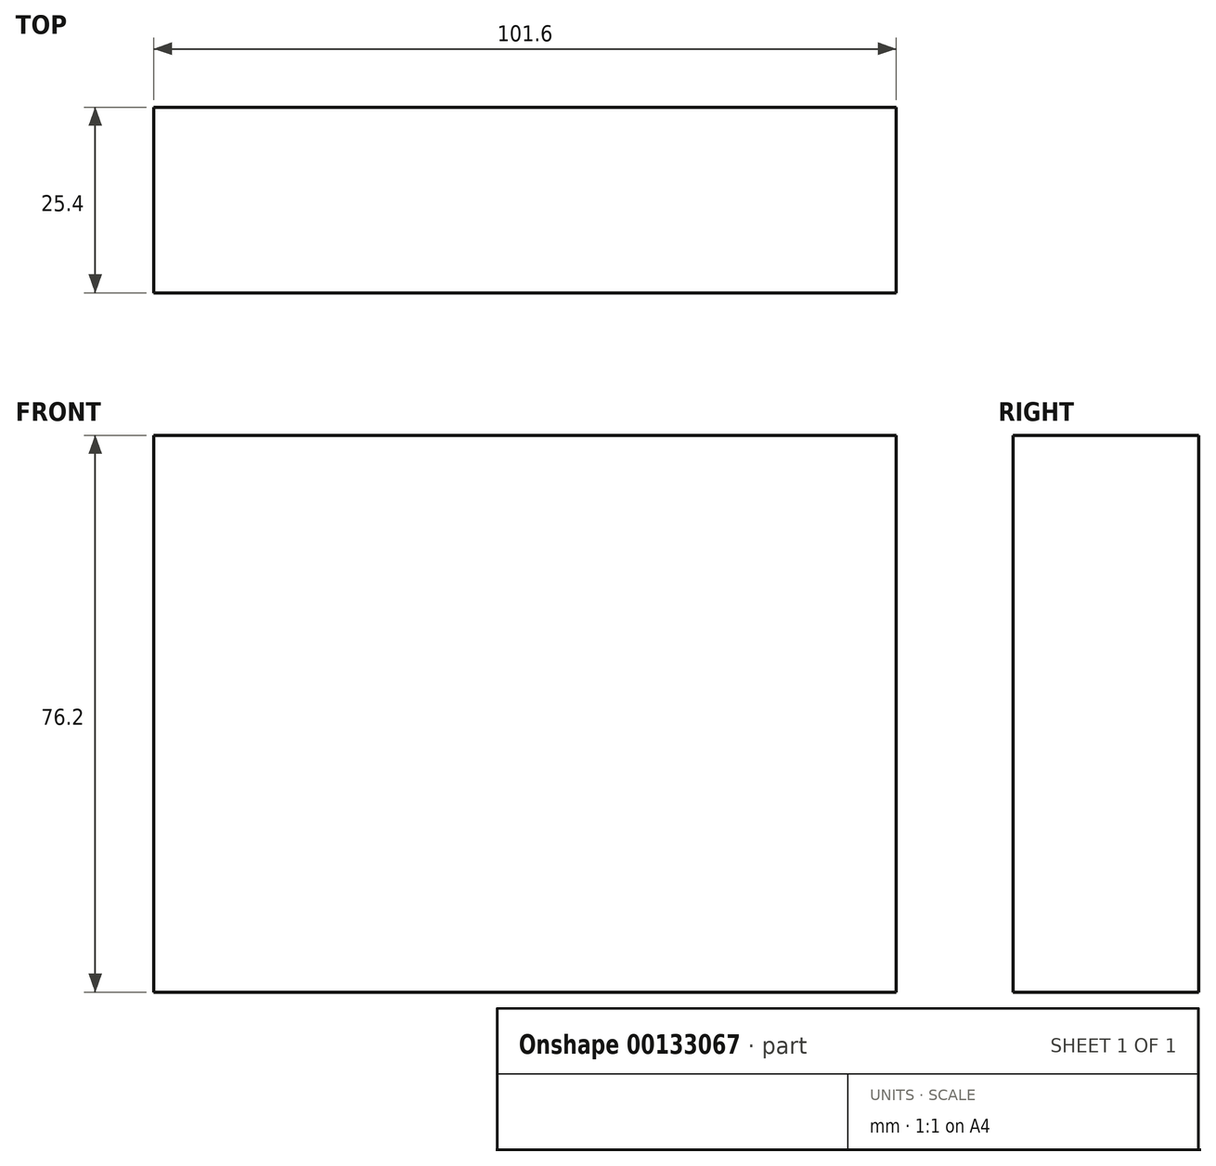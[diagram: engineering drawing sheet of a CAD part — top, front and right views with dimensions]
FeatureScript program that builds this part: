
annotation { "Feature Type Name" : "Feature", "Feature Type Description" : "" }
export const myFeature = defineFeature(function(context is Context, id is Id, definition is map)
    precondition{}
    {
        {
            var Q0;
            Q0=qCreatedBy(makeId("Front.planeOp"),FACE);
            var sketch = newSketch(context, id + "F0", { "sketchPlane" : qUnion([Q0])});
            skLineSegment(sketch, "E0.bottom", {"start": v(39.86, -22.03) * mm, "end": v(-61.74, -22.03) * mm});
            skLineSegment(sketch, "E0.top", {"start": v(39.86, 54.17) * mm, "end": v(-61.74, 54.17) * mm});
            skLineSegment(sketch, "E0.left", {"start": v(39.86, -22.03) * mm, "end": v(39.86, 54.17) * mm});
            skLineSegment(sketch, "E0.right", {"start": v(-61.74, -22.03) * mm, "end": v(-61.74, 54.17) * mm});
            skSolve(sketch);
        }
        {
            var Q0;
            Q0=makeQuery(id+"F0.imprint","IMPRINT",FACE,{"disambiguationData":[TD([[makeQuery(id+"F0.imprint","IMPRINT",EDGE,{"derivedFrom":sQuery(id+"F0.wireOp",EDGE,"E0.bottom")}),-1.0]])]});
            extrude(context, id + "F1", {"entities" : qUnion([Q0]), "endBound" : BoundingType.SYMMETRIC, "depth" : 25.4 * mm});
        }
    });
